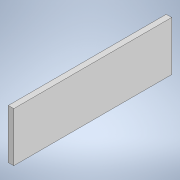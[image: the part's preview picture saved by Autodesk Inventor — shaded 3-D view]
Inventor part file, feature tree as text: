
AUTODESK INVENTOR PART (.ipt)
format: ipt  version: 2021 (Build 250183000, 183)  size: 88,576 bytes
history: native  units: in
note: dims shown in document units (in); Inventor stores cm internally (conversion verified against a paired STEP export)
features: extrude x1, sketch x1
ambient origin geometry x8: Origin, YZ Plane, XZ Plane, XY Plane, X Axis, Y Axis, Z Axis, Center Point
bodies: Solid1 (feature_tree)
feature tree (2):
  extrude  "Extrusion1"  Depth=7.1875in
  sketch  "Sketch1"  dims[d0=2.25in d1=7.1875in d2=0.25in d3=0.0in]
